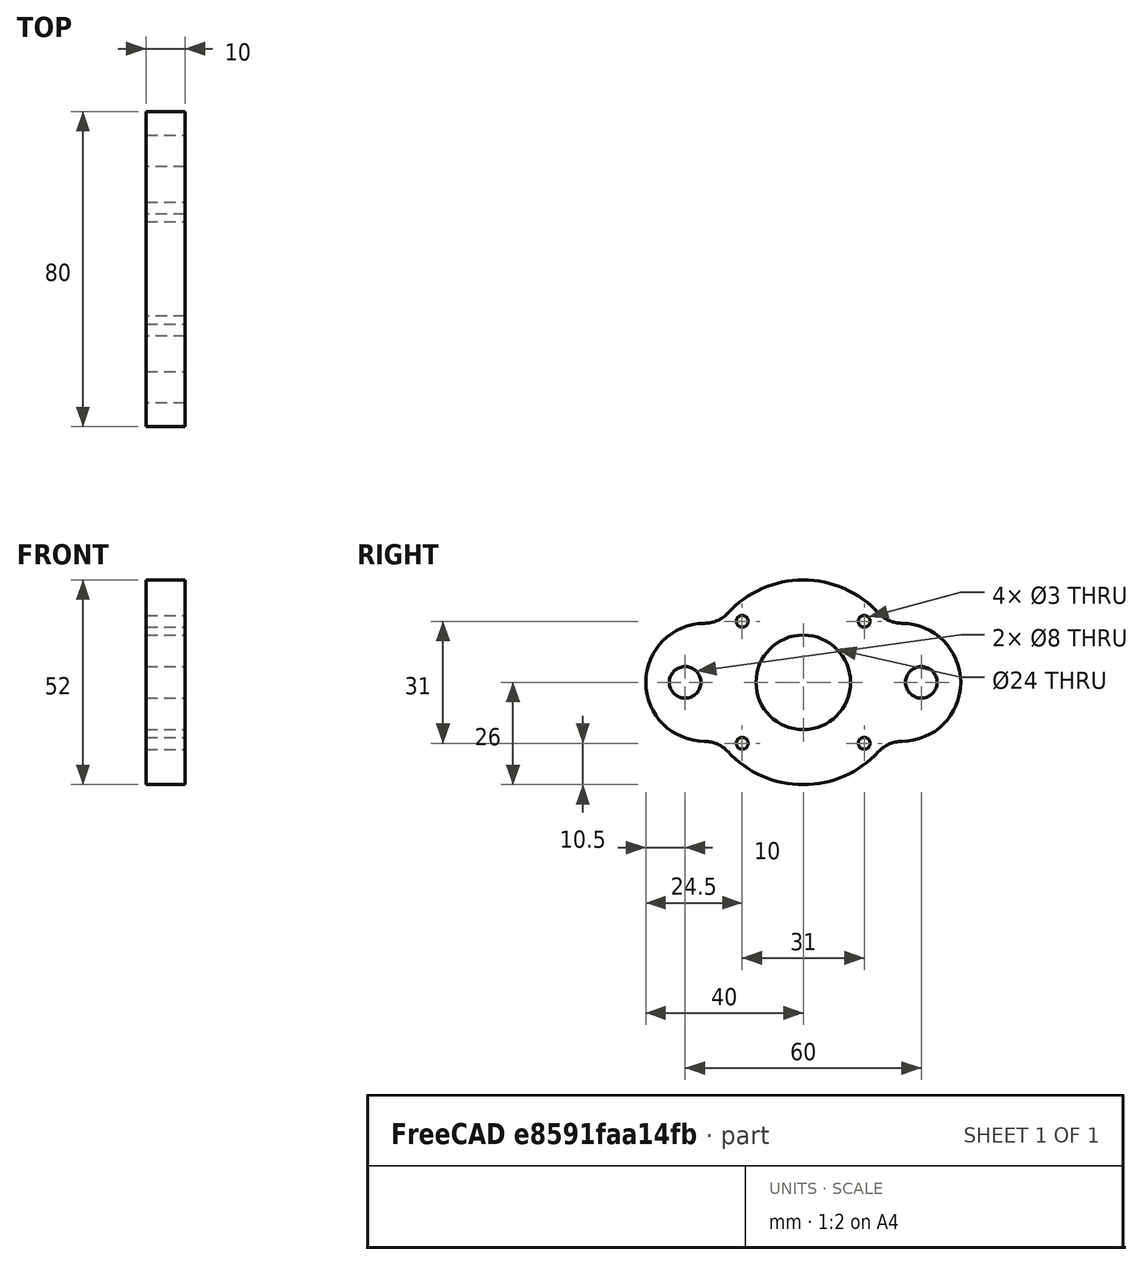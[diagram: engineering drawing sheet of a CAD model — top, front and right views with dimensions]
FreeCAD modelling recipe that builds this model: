
FCSTD DOCUMENT  (FreeCAD 0.16R6707 (Git))
Label: MotorMount
License: All rights reserved
LicenseURL: http://en.wikipedia.org/wiki/All_rights_reserved
objects: Sketcher::SketchObject×1, PartDesign::Pad×1
note: 3 computed .brp shape members not serialized (recipe doc carries the construction recipe); baked Part::Feature solids carry a one-line shape summary decoded from their .brp

FEATURE [Sketcher::SketchObject] Sketch018
  Placement = pos=(0,0,0) rot=(0.57735,-0.57735,-0.57735;2.0944rad)
  sketch-geometry (15):
    g0: ArcOfCircle CenterX=0 CenterY=0 CenterZ=0 NormalX=0 NormalY=0 NormalZ=1 Radius=26 StartAngle=0.742959 EndAngle=2.39863
    g1: ArcOfCircle CenterX=0 CenterY=0 CenterZ=0 NormalX=0 NormalY=0 NormalZ=1 Radius=26 StartAngle=3.88455 EndAngle=5.54023
    g2: ArcOfCircle CenterX=25 CenterY=0 CenterZ=0 NormalX=0 NormalY=0 NormalZ=1 Radius=15 StartAngle=4.71413 EndAngle=7.85224
    g3: ArcOfCircle CenterX=-25 CenterY=0 CenterZ=0 NormalX=0 NormalY=0 NormalZ=1 Radius=15 StartAngle=1.57254 EndAngle=4.71065
    g4: ArcOfCircle CenterX=-25.04 CenterY=23 CenterZ=0 NormalX=0 NormalY=0 NormalZ=1 Radius=8 StartAngle=4.71413 EndAngle=5.54023
    g5: ArcOfCircle CenterX=-25.04 CenterY=-23 CenterZ=0 NormalX=0 NormalY=0 NormalZ=1 Radius=8 StartAngle=0.742956 EndAngle=1.56906
    g6: ArcOfCircle CenterX=25.04 CenterY=23 CenterZ=0 NormalX=0 NormalY=0 NormalZ=1 Radius=8 StartAngle=3.88455 EndAngle=4.71065
    g7: ArcOfCircle CenterX=25.04 CenterY=-23 CenterZ=0 NormalX=0 NormalY=0 NormalZ=1 Radius=8 StartAngle=1.57253 EndAngle=2.39864
    g8: Circle CenterX=-30 CenterY=0 CenterZ=0 NormalX=0 NormalY=0 NormalZ=1 Radius=4
    g9: Circle CenterX=30 CenterY=0 CenterZ=0 NormalX=0 NormalY=0 NormalZ=1 Radius=4
    g10: Circle CenterX=-15.5 CenterY=15.5 CenterZ=0 NormalX=0 NormalY=0 NormalZ=1 Radius=1.5
    g11: Circle CenterX=15.5 CenterY=15.5 CenterZ=0 NormalX=0 NormalY=0 NormalZ=1 Radius=1.5
    g12: Circle CenterX=-15.5 CenterY=-15.5 CenterZ=0 NormalX=0 NormalY=0 NormalZ=1 Radius=1.5
    g13: Circle CenterX=15.5 CenterY=-15.5 CenterZ=0 NormalX=0 NormalY=0 NormalZ=1 Radius=1.5
    g14: Circle CenterX=0 CenterY=0 CenterZ=0 NormalX=0 NormalY=0 NormalZ=1 Radius=12
  constraints (48):
    c: Coincident(g7,g1)
    c: Coincident(g7,g2)
    c: Coincident(g2,g6)
    c: Coincident(g6,g0)
    c: Coincident(g0,g4)
    c: Coincident(g4,g3)
    c: Coincident(g3,g5)
    c: Coincident(g5,g1)
    c: Tangent(g5,g1)
    c: Tangent(g5,g3)
    c: Tangent(g4,g3)
    c: Tangent(g4,g0)
    c: Tangent(g6,g0)
    c: Tangent(g6,g2)
    c: Tangent(g2,g7)
    c: Tangent(g1,g7)
    c: Coincident(g0,g1)
    c: Symmetric(g3,g2,g0)
    c: Equal(g2,g3)
    c: Equal(g0,g1)
    c: Equal(g7,g6)
    c: Equal(g6,g4)
    c: Equal(g4,g5)
    c: Coincident(g0,g-1)
    c: Radius(g9) = 4
    c: Equal(g9,g8)
    c: Symmetric(g8,g9,g-1)
    c: PointOnObject(g9,g-1)
    c: PointOnObject(g2,g-1)
    c: DistanceX(g8,g9) = 60
    c: Radius(g2) = 15
    c: DistanceX(g-1,g2) = 25
    c: Coincident(g14,g-1)
    c: DistanceX(g10,g11) = 31
    c: DistanceY(g12,g10) = 31
    c: Symmetric(g10,g11,g-2)
    c: Symmetric(g12,g13,g-2)
    c: Symmetric(g13,g11,g-1)
    c: Radius(g14) = 12
    c: Radius(g11) = 1.5
    c: Equal(g11,g10)
    c: Equal(g11,g12)
    c: Equal(g11,g13)
    c: Symmetric(g6,g4,g-2)
    c: Symmetric(g7,g5,g-2)
    c: Symmetric(g4,g5,g-1)
    c: Radius(g0) = 26
    c: Radius(g4) = 8
FEATURE [PartDesign::Pad] Pad
  Length = 10
  Length2 = 100
  Placement = pos=(0,0,0) rot=(0.57735,-0.57735,-0.57735;2.0944rad)
  Sketch = -> Sketch018
  Type = 0
